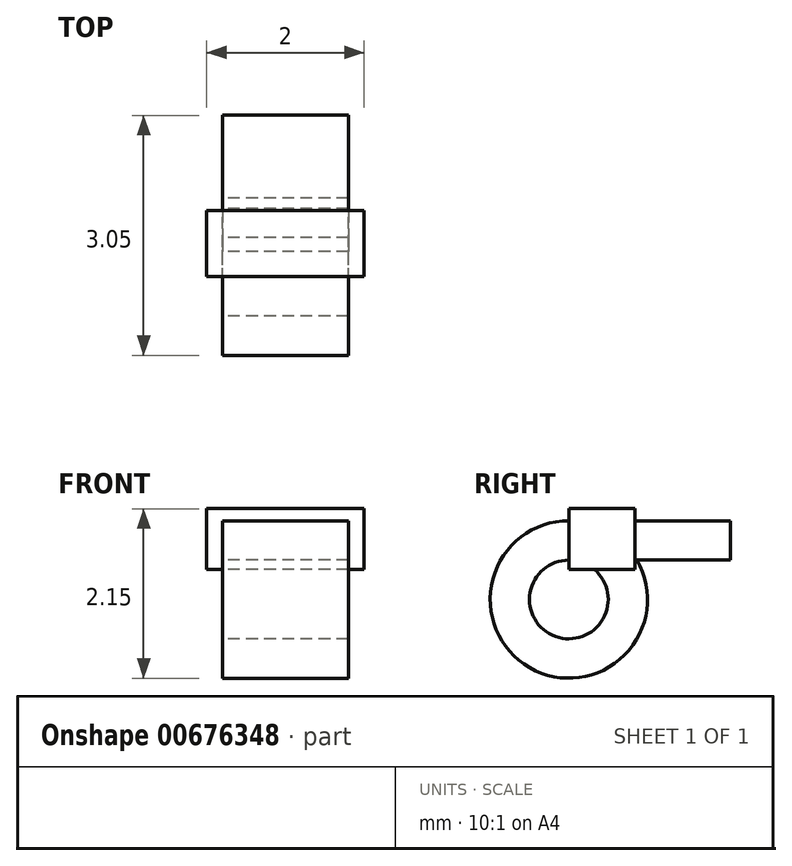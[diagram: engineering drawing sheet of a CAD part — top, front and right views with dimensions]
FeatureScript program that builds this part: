
annotation { "Feature Type Name" : "Feature", "Feature Type Description" : "" }
export const myFeature = defineFeature(function(context is Context, id is Id, definition is map)
    precondition{}
    {
        {
            var Q0;
            Q0=qCreatedBy(makeId("Right.planeOp"),FACE);
            var sketch = newSketch(context, id + "F0", { "sketchPlane" : qUnion([Q0])});
            skCircle(sketch, "E0", {"center": v(0, 0) * mm, "radius": 0.5 * mm});
            skArc(sketch, "E1", {"start": v(0, 1) * mm, "mid": v(-0.5, -0.87) * mm, "end": v(0.87, 0.5) * mm});
            skLineSegment(sketch, "E2", {"start": v(0.87, 0.5) * mm, "end": v(2.05, 0.5) * mm});
            skLineSegment(sketch, "E3", {"start": v(1.22, 1) * mm, "end": v(2.05, 1) * mm});
            skLineSegment(sketch, "E4", {"start": v(2.05, 1) * mm, "end": v(2.05, 0.5) * mm});
            skPoint(sketch, "E5.orphan", {"position": v(0, 0.5) * mm});
            skLineSegment(sketch, "E6", {"start": v(0, 1) * mm, "end": v(1.22, 1) * mm});
            skLineSegment(sketch, "E7.bottom", {"start": v(0, 1.15) * mm, "end": v(0.84, 1.15) * mm});
            skLineSegment(sketch, "E7.top", {"start": v(0, 0.38) * mm, "end": v(0.84, 0.38) * mm});
            skLineSegment(sketch, "E7.left", {"start": v(0, 1.15) * mm, "end": v(0, 0.38) * mm});
            skLineSegment(sketch, "E7.right", {"start": v(0.84, 1.15) * mm, "end": v(0.84, 0.38) * mm});
            skSolve(sketch);
        }
        {
            var Q0;
            {var subQ6=sQuery(id+"F0.wireOp",EDGE,"E1");Q0=makeQuery(id+"F0.imprint","IMPRINT",FACE,{"disambiguationData":[TD([[makeQuery(id+"F0.imprint","IMPRINT",EDGE,{"derivedFrom":subQ6}),1.0]])]});}
            var Q1;
            {var subQ3=sQuery(id+"F0.wireOp",EDGE,"E0");var subQ7=sQuery(id+"F0.wireOp",EDGE,"E7.top");var subQ9=makeQuery(id+"F0.imprint","INTERSECT",VERTEX,{"derivedFrom":[subQ3,subQ7]});Q1=makeQuery(id+"F0.imprint","IMPRINT",FACE,{"disambiguationData":[TD([[makeQuery(id+"F0.imprint","IMPRINT",EDGE,{"disambiguationData":[TD([[subQ9,-1.0]])],"derivedFrom":subQ3}),-1.0]])]});}
            extrude(context, id + "F1", {"entities" : qUnion([Q0, Q1]), "depth" : 1.6 * mm, "offsetDistance" : 25 * mm, "symmetric" : true});
        }
        {
            var Q0;
            {var subQ5=sQuery(id+"F0.wireOp",EDGE,"E7.bottom");Q0=makeQuery(id+"F0.imprint","IMPRINT",FACE,{"disambiguationData":[TD([[makeQuery(id+"F0.imprint","IMPRINT",EDGE,{"derivedFrom":subQ5}),-1.0]])]});}
            var Q1;
            {var subQ0=sQuery(id+"F0.wireOp",EDGE,"E7.top");var subQ1=sQuery(id+"F0.wireOp",EDGE,"E0");var subQ2=makeQuery(id+"F0.imprint","INTERSECT",VERTEX,{"derivedFrom":[subQ1,subQ0]});Q1=makeQuery(id+"F0.imprint","IMPRINT",FACE,{"disambiguationData":[TD([[makeQuery(id+"F0.imprint","IMPRINT",EDGE,{"disambiguationData":[TD([[subQ2,-1.0]])],"derivedFrom":subQ1}),1.0]])]});}
            var Q2;
            {var subQ3=sQuery(id+"F0.wireOp",EDGE,"E0");var subQ7=sQuery(id+"F0.wireOp",EDGE,"E7.top");var subQ9=makeQuery(id+"F0.imprint","INTERSECT",VERTEX,{"derivedFrom":[subQ3,subQ7]});Q2=makeQuery(id+"F0.imprint","IMPRINT",FACE,{"disambiguationData":[TD([[makeQuery(id+"F0.imprint","IMPRINT",EDGE,{"disambiguationData":[TD([[subQ9,-1.0]])],"derivedFrom":subQ3}),-1.0]])]});}
            extrude(context, id + "F2", {"entities" : qUnion([Q0, Q1, Q2]), "operationType" : NewBodyOperationType.ADD, "depth" : 2 * mm, "offsetDistance" : 25 * mm, "symmetric" : true});
        }
    });
